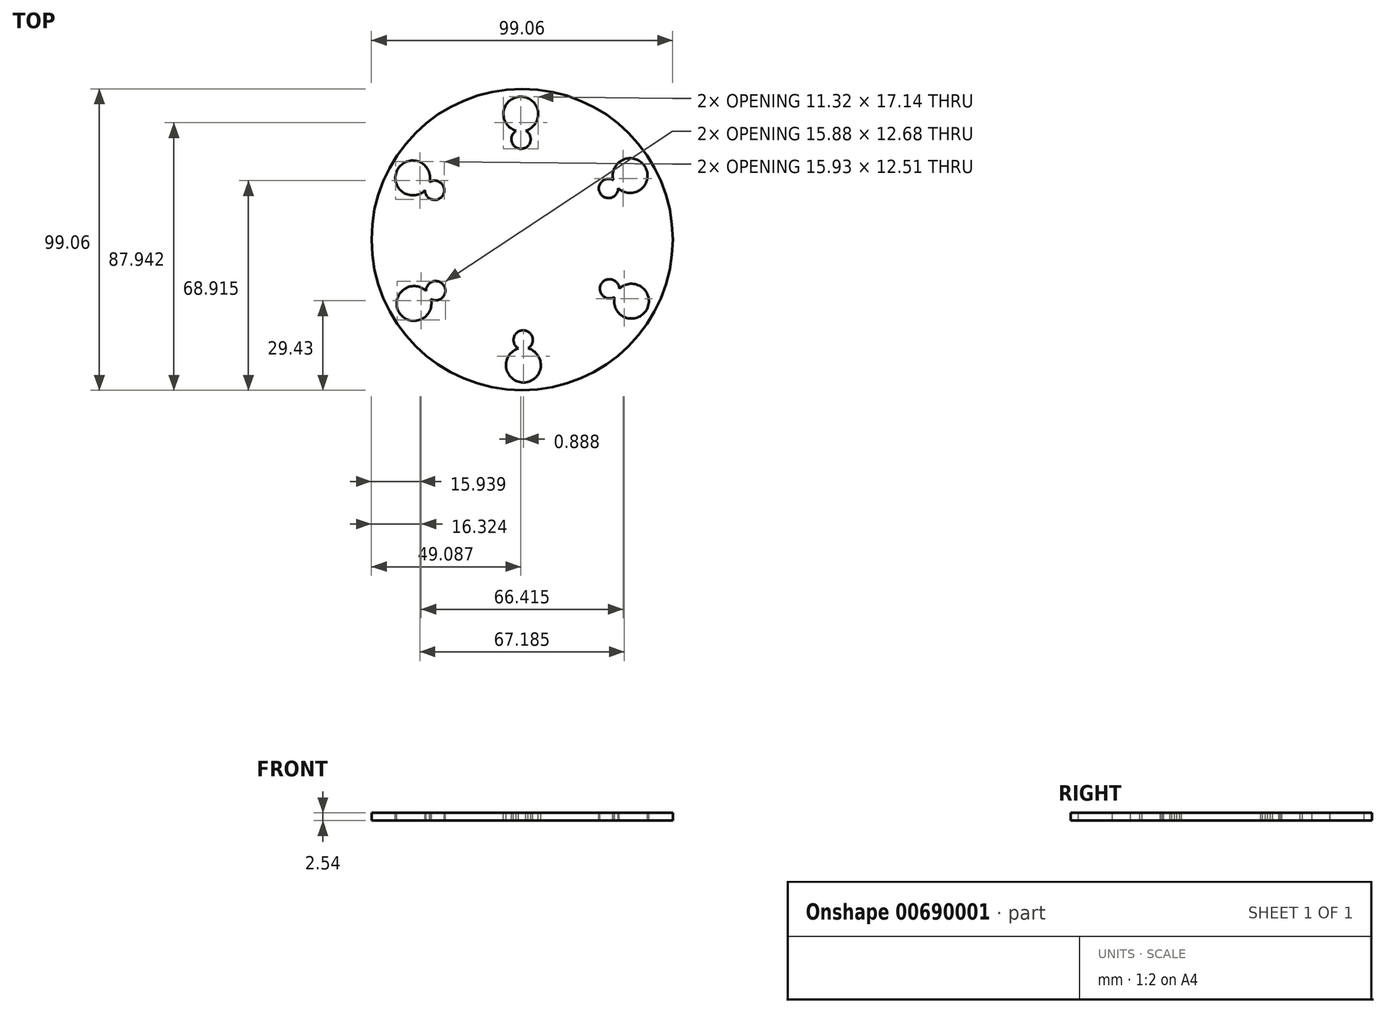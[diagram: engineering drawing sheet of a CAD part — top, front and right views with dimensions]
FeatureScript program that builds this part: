
annotation { "Feature Type Name" : "Feature", "Feature Type Description" : "" }
export const myFeature = defineFeature(function(context is Context, id is Id, definition is map)
    precondition{}
    {
        {
            var Q0;
            Q0=qCreatedBy(makeId("Top.planeOp"),FACE);
            var sketch = newSketch(context, id + "F0", { "sketchPlane" : qUnion([Q0])});
            skCircle(sketch, "E0", {"center": v(0.11, -0.33) * mm, "radius": 49.53 * mm});
            skCircle(sketch, "E1.cCircle", {"center": v(0.11, -0.33) * mm, "radius": 49.53 * mm, "construction": true});
            skCircle(sketch, "E2", {"center": v(28.88, -16.54) * mm, "radius": 16.51 * mm});
            skCircle(sketch, "E3", {"center": v(0.46, -33.35) * mm, "radius": 16.5 * mm});
            skCircle(sketch, "E4", {"center": v(-28.3, -17.14) * mm, "radius": 16.5 * mm});
            skCircle(sketch, "E5", {"center": v(-28.66, 15.87) * mm, "radius": 16.5 * mm});
            skCircle(sketch, "E6", {"center": v(-0.24, 32.68) * mm, "radius": 16.51 * mm});
            skCircle(sketch, "E7", {"center": v(28.53, 16.48) * mm, "radius": 16.51 * mm});
            skPoint(sketch, "E8", {"position": v(-0.32, 40.94) * mm});
            skPoint(sketch, "E9", {"position": v(35.64, 20.68) * mm});
            skPoint(sketch, "E10", {"position": v(36.07, -20.6) * mm});
            skPoint(sketch, "E11", {"position": v(0.55, -41.6) * mm});
            skPoint(sketch, "E12", {"position": v(-35.41, -21.35) * mm});
            skPoint(sketch, "E13", {"position": v(-35.85, 19.93) * mm});
            skSolve(sketch);
        }
        {
            var Q0;
            {var subQ0=sQuery(id+"F0.wireOp",EDGE,"E6");var subQ1=sQuery(id+"F0.wireOp",EDGE,"E0");var subQ2=makeQuery(id+"F0.imprint","INTERSECT",VERTEX,{"derivedFrom":[subQ1,subQ0]});Q0=makeQuery(id+"F0.imprint","IMPRINT",FACE,{"disambiguationData":[TD([[makeQuery(id+"F0.imprint","IMPRINT",EDGE,{"disambiguationData":[TD([[subQ2,1.0]])],"derivedFrom":subQ1}),1.0]])]});}
            var Q1;
            {var subQ0=sQuery(id+"F0.wireOp",EDGE,"E6");var subQ1=sQuery(id+"F0.wireOp",EDGE,"E0");var subQ2=makeQuery(id+"F0.imprint","INTERSECT",VERTEX,{"derivedFrom":[subQ1,subQ0]});Q1=makeQuery(id+"F0.imprint","IMPRINT",FACE,{"disambiguationData":[TD([[makeQuery(id+"F0.imprint","IMPRINT",EDGE,{"disambiguationData":[TD([[subQ2,-1.0]])],"derivedFrom":subQ1}),1.0]])]});}
            var Q2;
            {var subQ0=sQuery(id+"F0.wireOp",EDGE,"E5");var subQ1=sQuery(id+"F0.wireOp",EDGE,"E0");var subQ2=makeQuery(id+"F0.imprint","INTERSECT",VERTEX,{"derivedFrom":[subQ1,subQ0]});Q2=makeQuery(id+"F0.imprint","IMPRINT",FACE,{"disambiguationData":[TD([[makeQuery(id+"F0.imprint","IMPRINT",EDGE,{"disambiguationData":[TD([[subQ2,-1.0]])],"derivedFrom":subQ1}),1.0]])]});}
            var Q3;
            {var subQ0=sQuery(id+"F0.wireOp",EDGE,"E4");var subQ1=sQuery(id+"F0.wireOp",EDGE,"E0");var subQ2=makeQuery(id+"F0.imprint","INTERSECT",VERTEX,{"derivedFrom":[subQ1,subQ0]});Q3=makeQuery(id+"F0.imprint","IMPRINT",FACE,{"disambiguationData":[TD([[makeQuery(id+"F0.imprint","IMPRINT",EDGE,{"disambiguationData":[TD([[subQ2,-1.0]])],"derivedFrom":subQ1}),1.0]])]});}
            var Q4;
            {var subQ0=sQuery(id+"F0.wireOp",EDGE,"E3");var subQ1=sQuery(id+"F0.wireOp",EDGE,"E0");var subQ2=makeQuery(id+"F0.imprint","INTERSECT",VERTEX,{"derivedFrom":[subQ1,subQ0]});Q4=makeQuery(id+"F0.imprint","IMPRINT",FACE,{"disambiguationData":[TD([[makeQuery(id+"F0.imprint","IMPRINT",EDGE,{"disambiguationData":[TD([[subQ2,-1.0]])],"derivedFrom":subQ1}),1.0]])]});}
            var Q5;
            {var subQ0=sQuery(id+"F0.wireOp",EDGE,"E7");var subQ1=sQuery(id+"F0.wireOp",EDGE,"E0");var subQ2=makeQuery(id+"F0.imprint","INTERSECT",VERTEX,{"derivedFrom":[subQ1,subQ0]});Q5=makeQuery(id+"F0.imprint","IMPRINT",FACE,{"disambiguationData":[TD([[makeQuery(id+"F0.imprint","IMPRINT",EDGE,{"disambiguationData":[TD([[subQ2,1.0]])],"derivedFrom":subQ1}),1.0]])]});}
            var Q6;
            {var subQ0=sQuery(id+"F0.wireOp",EDGE,"E2");var subQ1=makeQuery(id+"F0.imprint","INTERSECT",VERTEX,{"derivedFrom":[subQ0,sQuery(id+"F0.wireOp",EDGE,"E3")]});Q6=makeQuery(id+"F0.imprint","IMPRINT",FACE,{"disambiguationData":[TD([[makeQuery(id+"F0.imprint","IMPRINT",EDGE,{"disambiguationData":[TD([[subQ1,1.0]])],"derivedFrom":subQ0}),1.0]])]});}
            var Q7;
            {var subQ0=sQuery(id+"F0.wireOp",EDGE,"E3");var subQ1=makeQuery(id+"F0.imprint","INTERSECT",VERTEX,{"derivedFrom":[sQuery(id+"F0.wireOp",EDGE,"E2"),subQ0]});Q7=makeQuery(id+"F0.imprint","IMPRINT",FACE,{"disambiguationData":[TD([[makeQuery(id+"F0.imprint","IMPRINT",EDGE,{"disambiguationData":[TD([[subQ1,-1.0]])],"derivedFrom":subQ0}),1.0]])]});}
            var Q8;
            {var subQ0=sQuery(id+"F0.wireOp",EDGE,"E4");var subQ1=makeQuery(id+"F0.imprint","INTERSECT",VERTEX,{"derivedFrom":[sQuery(id+"F0.wireOp",EDGE,"E0"),subQ0]});Q8=makeQuery(id+"F0.imprint","IMPRINT",FACE,{"disambiguationData":[TD([[makeQuery(id+"F0.imprint","IMPRINT",EDGE,{"disambiguationData":[TD([[subQ1,1.0]])],"derivedFrom":subQ0}),1.0]])]});}
            var Q9;
            {var subQ0=sQuery(id+"F0.wireOp",EDGE,"E5");var subQ1=makeQuery(id+"F0.imprint","INTERSECT",VERTEX,{"derivedFrom":[sQuery(id+"F0.wireOp",EDGE,"E0"),subQ0]});Q9=makeQuery(id+"F0.imprint","IMPRINT",FACE,{"disambiguationData":[TD([[makeQuery(id+"F0.imprint","IMPRINT",EDGE,{"disambiguationData":[TD([[subQ1,1.0]])],"derivedFrom":subQ0}),1.0]])]});}
            var Q10;
            {var subQ0=sQuery(id+"F0.wireOp",EDGE,"E6");var subQ1=makeQuery(id+"F0.imprint","INTERSECT",VERTEX,{"derivedFrom":[sQuery(id+"F0.wireOp",EDGE,"E0"),subQ0]});Q10=makeQuery(id+"F0.imprint","IMPRINT",FACE,{"disambiguationData":[TD([[makeQuery(id+"F0.imprint","IMPRINT",EDGE,{"disambiguationData":[TD([[subQ1,-1.0]])],"derivedFrom":subQ0}),1.0]])]});}
            var Q11;
            {var subQ0=sQuery(id+"F0.wireOp",EDGE,"E7");var subQ1=makeQuery(id+"F0.imprint","INTERSECT",VERTEX,{"derivedFrom":[sQuery(id+"F0.wireOp",EDGE,"E0"),subQ0]});Q11=makeQuery(id+"F0.imprint","IMPRINT",FACE,{"disambiguationData":[TD([[makeQuery(id+"F0.imprint","IMPRINT",EDGE,{"disambiguationData":[TD([[subQ1,-1.0]])],"derivedFrom":subQ0}),1.0]])]});}
            var Q12;
            {var subQ5=sQuery(id+"F0.wireOp",EDGE,"E3");var subQ6=sQuery(id+"F0.wireOp",EDGE,"E2");var subQ7=makeQuery(id+"F0.imprint","INTERSECT",VERTEX,{"derivedFrom":[subQ6,subQ5]});Q12=makeQuery(id+"F0.imprint","IMPRINT",FACE,{"disambiguationData":[TD([[makeQuery(id+"F0.imprint","IMPRINT",EDGE,{"disambiguationData":[TD([[subQ7,1.0]])],"derivedFrom":subQ6}),-1.0]])]});}
            extrude(context, id + "F1", {"entities" : qUnion([Q0, Q1, Q2, Q3, Q4, Q5, Q6, Q7, Q8, Q9, Q10, Q11, Q12]), "oppositeDirection" : true, "depth" : 2.54 * mm, "offsetDistance" : 25.4 * mm});
        }
        {
            var Q0;
            Q0=sQuery(id+"F0.wireOp",VERTEX,"E8");
            var Q1;
            Q1=sQuery(id+"F0.wireOp",VERTEX,"E9");
            var Q2;
            Q2=sQuery(id+"F0.wireOp",VERTEX,"E10");
            var Q3;
            Q3=sQuery(id+"F0.wireOp",VERTEX,"E11");
            var Q4;
            Q4=sQuery(id+"F0.wireOp",VERTEX,"E12");
            var Q5;
            Q5=sQuery(id+"F0.wireOp",VERTEX,"E13");
            var Q6;
            Q6=makeQuery(id+"F1.opExtrude","SWEPT_BODY",BODY,{"disambiguationData":[OSD([sQuery(id+"F0.wireOp",EDGE,"E0")])]});
            hole(context, id + "F2", {"style" : HoleStyle.SIMPLE, "endStyle" : HoleEndStyle.THROUGH, "holeDiameter" : 11.43 * mm, "majorDiameter" : 6.35 * mm, "isTappedThrough" : true, "tappedDepth" : 12.7 * mm, "tapClearance" : 3, "locations" : qUnion([Q0, Q1, Q2, Q3, Q4, Q5]), "scope" : qUnion([Q6])});
        }
        {
            var Q0;
            Q0=sQuery(id+"F0.wireOp",VERTEX,"E5.center");
            var Q1;
            Q1=sQuery(id+"F0.wireOp",VERTEX,"E6.center");
            var Q2;
            Q2=sQuery(id+"F0.wireOp",VERTEX,"E7.center");
            var Q3;
            Q3=sQuery(id+"F0.wireOp",VERTEX,"E2.center");
            var Q4;
            Q4=sQuery(id+"F0.wireOp",VERTEX,"E3.center");
            var Q5;
            Q5=sQuery(id+"F0.wireOp",VERTEX,"E4.center");
            var Q6;
            Q6=makeQuery(id+"F1.opExtrude","SWEPT_BODY",BODY,{"disambiguationData":[OSD([sQuery(id+"F0.wireOp",EDGE,"E0")])]});
            hole(context, id + "F3", {"style" : HoleStyle.SIMPLE, "endStyle" : HoleEndStyle.THROUGH, "holeDiameter" : 6.35 * mm, "majorDiameter" : 6.35 * mm, "isTappedThrough" : true, "tappedDepth" : 12.7 * mm, "tapClearance" : 3, "locations" : qUnion([Q0, Q1, Q2, Q3, Q4, Q5]), "scope" : qUnion([Q6])});
        }
    });
